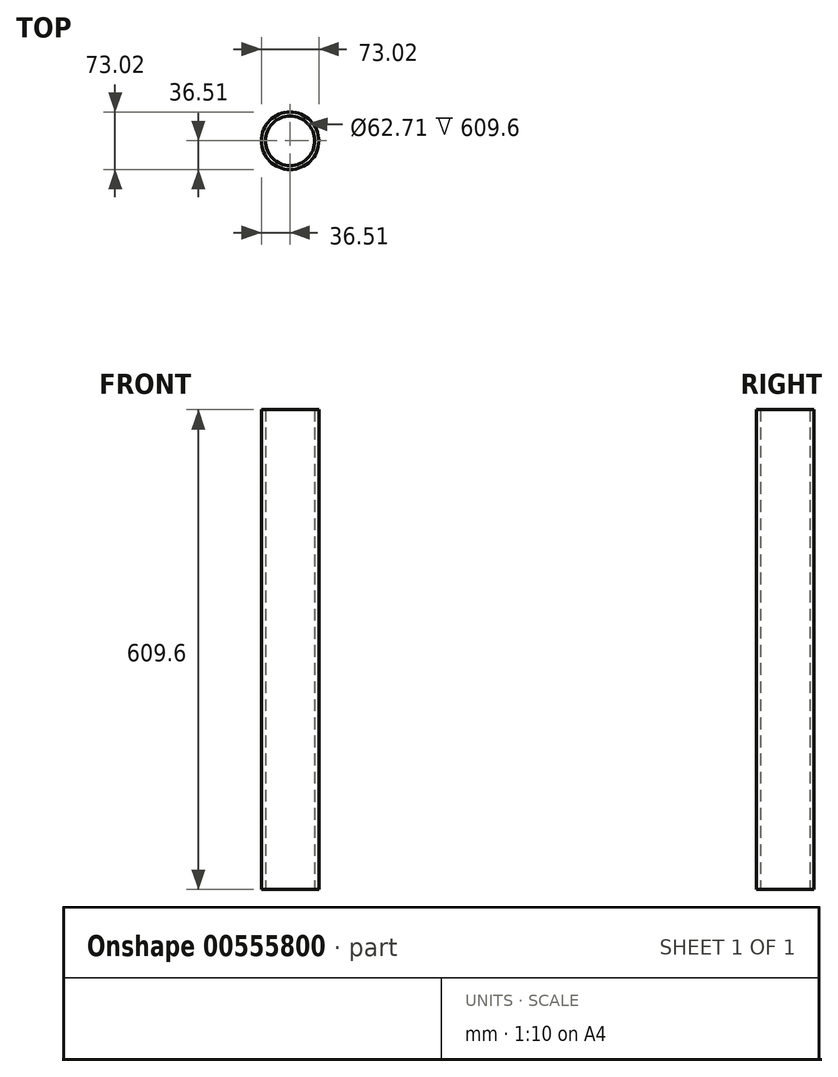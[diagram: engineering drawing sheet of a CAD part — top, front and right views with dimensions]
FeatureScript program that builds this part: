
annotation { "Feature Type Name" : "Feature", "Feature Type Description" : "" }
export const myFeature = defineFeature(function(context is Context, id is Id, definition is map)
    precondition{}
    {
        {
            var Q0;
            Q0=qCreatedBy(makeId("Top.planeOp"),FACE);
            var sketch = newSketch(context, id + "F0", { "sketchPlane" : qUnion([Q0])});
            skCircle(sketch, "E0", {"center": v(0, 0) * mm, "radius": 36.51 * mm});
            skCircle(sketch, "E1", {"center": v(0, 0) * mm, "radius": 31.36 * mm});
            skSolve(sketch);
        }
        {
            var Q0;
            Q0=qSketchRegion(id+"F0",true);
            extrude(context, id + "F1", {"entities" : qUnion([Q0]), "depth" : 609.6 * mm, "offsetDistance" : 25.4 * mm});
        }
    });
